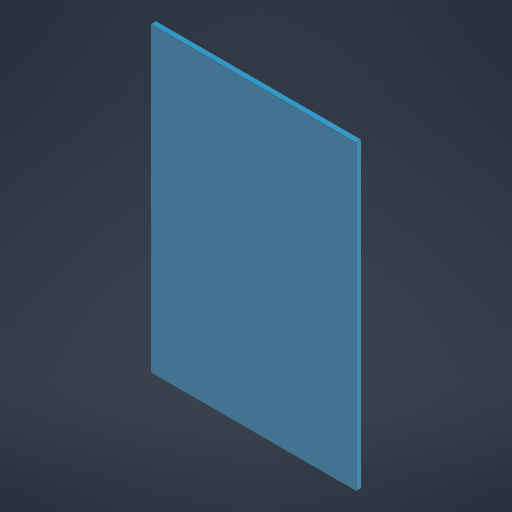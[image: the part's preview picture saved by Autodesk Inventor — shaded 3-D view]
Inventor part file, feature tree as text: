
AUTODESK INVENTOR PART (.ipt)
format: ipt  version: 2023 (Build 270158000, 158)  size: 160,256 bytes
history: native  units: mm
features: extrude x1, sketch x1
ambient origin geometry x8: Origin, YZ Plane, XZ Plane, XY Plane, X Axis, Y Axis, Z Axis, Center Point
bodies: Solid1 (feature_tree)
feature tree (2):
  extrude  "Extrusion1"  Depth=97.0mm
  sketch  "Sketch1"  dims[d0=66.0mm d1=97.0mm d2=1.66mm d3=0.0mm]
